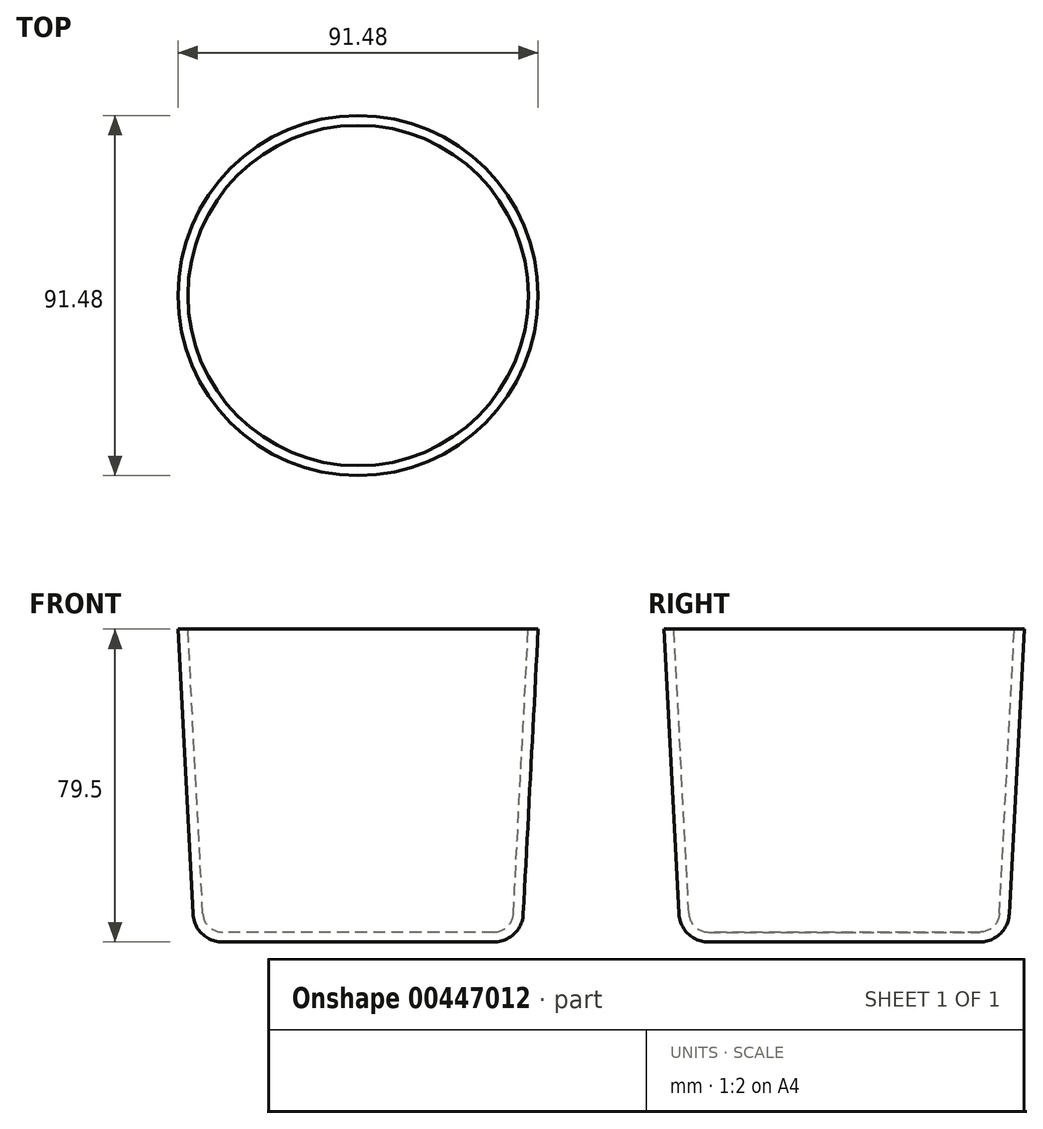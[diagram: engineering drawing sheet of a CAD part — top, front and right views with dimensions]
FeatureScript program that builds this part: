
annotation { "Feature Type Name" : "Feature", "Feature Type Description" : "" }
export const myFeature = defineFeature(function(context is Context, id is Id, definition is map)
    precondition{}
    {
        {
            var Q0;
            Q0=qCreatedBy(makeId("Top.planeOp"),FACE);
            var sketch = newSketch(context, id + "F0", { "sketchPlane" : qUnion([Q0])});
            skCircle(sketch, "E0", {"center": v(0, 0) * mm, "radius": 43.24 * mm});
            skSolve(sketch);
        }
        {
            var Q0;
            Q0=makeQuery(id+"F0.imprint","IMPRINT",FACE,{"disambiguationData":[TD([[makeQuery(id+"F0.imprint","IMPRINT",EDGE,{"derivedFrom":sQuery(id+"F0.wireOp",EDGE,"E0")}),1.0]])]});
            extrude(context, id + "F1", {"entities" : qUnion([Q0]), "oppositeDirection" : true, "depth" : 77 * mm, "hasDraft" : true, "draftAngle" : 3 * degree, "draftPullDirection" : true});
        }
        {
            var Q0;
            Q0=makeQuery(id+"F1.opExtrude","CAP_FACE",FACE,{"disambiguationData":[OSD([sQuery(id+"F0.wireOp",EDGE,"E0")])],"isStart":false});
            fillet(context, id + "F2", {"entities" : qUnion([Q0]), "radius" : 5 * mm, "tangentPropagation" : true, "allowEdgeOverflow" : false});
        }
        {
            var Q0;
            Q0=makeQuery(id+"F1.opExtrude","CAP_FACE",FACE,{"disambiguationData":[OSD([sQuery(id+"F0.wireOp",EDGE,"E0")])],"isStart":true});
            shell(context, id + "F3", {"entities" : qUnion([Q0]), "thickness" : 2.5 * mm, "oppositeDirection" : true});
        }
    });
